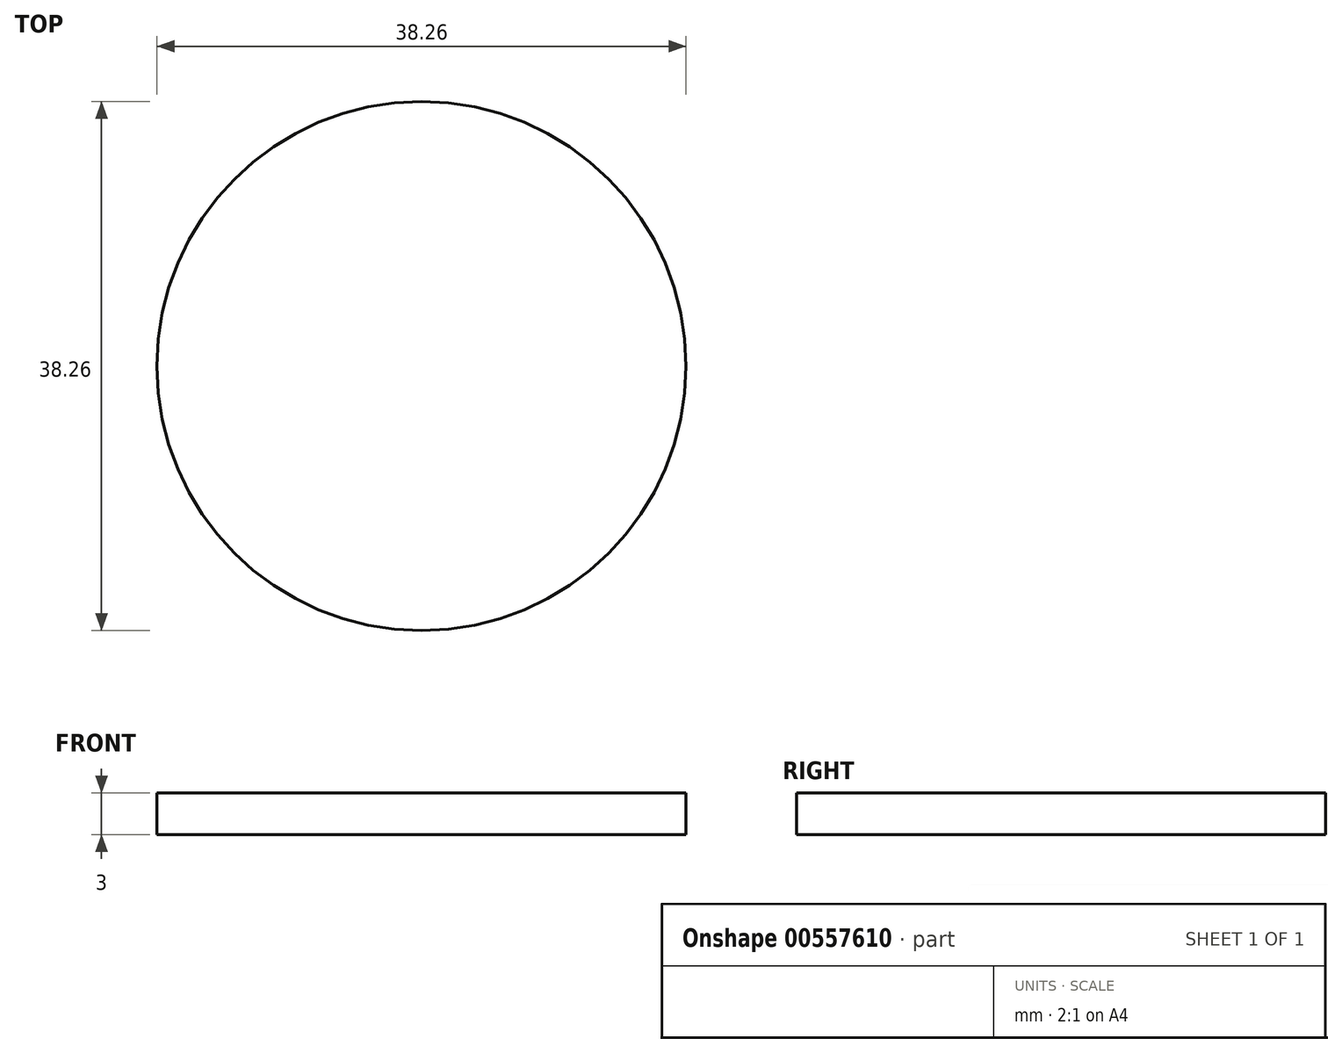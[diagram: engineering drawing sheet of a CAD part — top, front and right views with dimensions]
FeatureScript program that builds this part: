
annotation { "Feature Type Name" : "Feature", "Feature Type Description" : "" }
export const myFeature = defineFeature(function(context is Context, id is Id, definition is map)
    precondition{}
    {
        {
            var Q0;
            Q0=qCreatedBy(makeId("Top.planeOp"),FACE);
            var sketch = newSketch(context, id + "F0", { "sketchPlane" : qUnion([Q0])});
            skCircle(sketch, "E0", {"center": v(0, 0) * mm, "radius": 19.13 * mm});
            skSolve(sketch);
        }
        {
            var Q0;
            Q0 = qSketchRegion(id + "F0", true);
            extrude(context, id + "F1", {"entities" : qUnion([Q0]), "endBound" : BoundingType.SYMMETRIC, "depth" : 3 * mm, "offsetDistance" : 25.4 * mm});
        }
    });
